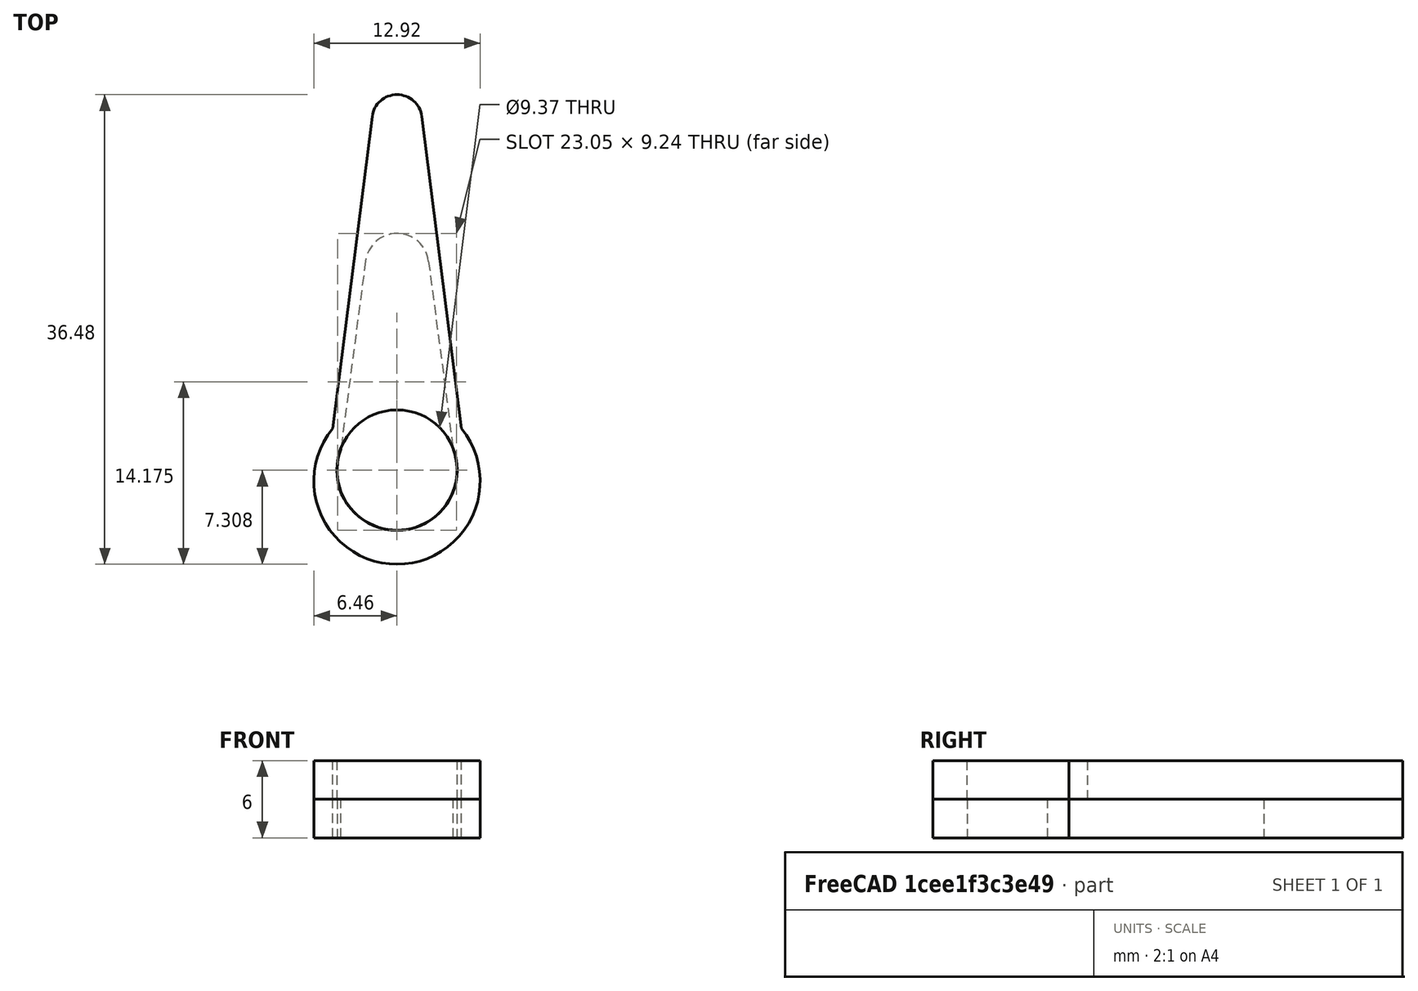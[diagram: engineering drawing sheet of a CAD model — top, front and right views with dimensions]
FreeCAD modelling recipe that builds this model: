
FCSTD DOCUMENT  (FreeCAD 0.18.4R)
Label: servo_pointer
License: All rights reserved
LicenseURL: http://en.wikipedia.org/wiki/All_rights_reserved
objects: Sketcher::SketchObject×2, PartDesign::Pad×2, PartDesign::Body×2, Mesh::Feature×1, Part::Compound×1, App::Part×1
note: 9 computed .brp shape members not serialized (recipe doc carries the construction recipe); baked Part::Feature solids carry a one-line shape summary decoded from their .brp

FEATURE [Mesh::Feature] ServoNeedle_Hole  label="ServoNeedle-Hole"
  Placement = pos=(0,0,2) rot=(0,0,1;0rad)
FEATURE [Sketcher::SketchObject] Sketch
  MapMode = 5
  Support = -> [XY_Plane001]
  sketch-geometry (8):
    g0: LineSegment StartX=-2.44767 StartY=16.3215 StartZ=0 EndX=-4.37 EndY=1.69 EndZ=0
    g1: LineSegment StartX=2.44767 StartY=16.3215 StartZ=0 EndX=4.37 EndY=1.69 EndZ=0
    g2: ArcOfCircle CenterX=2e-16 CenterY=0.0782726 CenterZ=0 NormalX=0 NormalY=0 NormalZ=1 AngleXU=0 Radius=4.65774 StartAngle=2.78825 EndAngle=6.63652
    g3: ArcOfCircle CenterX=1e-16 CenterY=15.9999 CenterZ=0 NormalX=0 NormalY=0 NormalZ=1 AngleXU=0 Radius=2.4687 StartAngle=0.130635 EndAngle=3.01096
    g4: ArcOfCircle CenterX=-3e-16 CenterY=-0.77104 CenterZ=0 NormalX=0 NormalY=0 NormalZ=1 AngleXU=0 Radius=6.46039 StartAngle=2.45585 EndAngle=6.96893
    g5: LineSegment StartX=-1.92828 StartY=27.554 StartZ=0 EndX=-5 EndY=3.32 EndZ=0
    g6: ArcOfCircle CenterX=-1e-16 CenterY=27.3096 CenterZ=0 NormalX=0 NormalY=0 NormalZ=1 AngleXU=0 Radius=1.94371 StartAngle=0.12608 EndAngle=3.01551
    g7: LineSegment StartX=1.92828 StartY=27.554 StartZ=0 EndX=5 EndY=3.32 EndZ=0
  constraints (16):
    c: Symmetric(g1,g0,g-2)
    c: Symmetric(g1,g0,g-2)
    c: Coincident(g2,g1)
    c: Coincident(g2,g0)
    c: Coincident(g3,g0)
    c: Tangent(g3,g1) = 1.5708
    c: Coincident(g4,g7)
    c: Coincident(g4,g5)
    c: Coincident(g6,g5)
    c: Tangent(g6,g7) = 1.5708
    c: Symmetric(g5,g6,g-2)
    c: Symmetric(g4,g4,g-2)
    c: DistanceX(g2,g4) = 5
    c: DistanceX(g2,g1) = 4.37
    c: DistanceY(g-1,g1) = 1.69
    c: DistanceY(g-1,g4) = 3.32
FEATURE [PartDesign::Pad] Pad
  Length = 3
  Length2 = 100
  Profile = -> Sketch
  Type = 0
FEATURE [PartDesign::Body] Body
  Group = -> [Sketch,Pad]
  Origin = -> Origin001
  Tip = -> Pad
FEATURE [Sketcher::SketchObject] Sketch001
  MapMode = 5
  Support = -> [XY_Plane001]
  sketch-geometry (5):
    g0: ArcOfCircle CenterX=-5e-16 CenterY=-0.77104 CenterZ=0 NormalX=0 NormalY=0 NormalZ=1 AngleXU=0 Radius=6.46039 StartAngle=2.45585 EndAngle=6.96893
    g1: LineSegment StartX=-1.92828 StartY=27.554 StartZ=0 EndX=-5 EndY=3.32 EndZ=0
    g2: ArcOfCircle CenterX=1e-16 CenterY=27.3096 CenterZ=0 NormalX=0 NormalY=0 NormalZ=1 AngleXU=0 Radius=1.94371 StartAngle=0.12608 EndAngle=3.01551
    g3: LineSegment StartX=1.92828 StartY=27.554 StartZ=0 EndX=5 EndY=3.32 EndZ=0
    g4: Circle CenterX=-2e-16 CenterY=0.0782726 CenterZ=0 NormalX=0 NormalY=0 NormalZ=1 AngleXU=0 Radius=4.68435
  constraints (7):
    c: Coincident(g0,g3)
    c: Coincident(g0,g1)
    c: Coincident(g2,g1)
    c: Tangent(g2,g3) = 1.5708
    c: Symmetric(g1,g2,g-2)
    c: Symmetric(g0,g0,g-2)
    c: DistanceY(g-1,g0) = 3.32
FEATURE [PartDesign::Pad] Pad001
  Length = 3
  Length2 = 100
  Profile = -> Sketch001
  Type = 0
FEATURE [PartDesign::Body] Body001
  Group = -> [Sketch001,Pad001]
  Origin = -> Origin002
  Placement = pos=(0,0,3) rot=(0,0,1;0rad)
  Tip = -> Pad001
FEATURE [Part::Compound] Compound
  Links = -> [Body001,Body]
FEATURE [App::Part] Part001  label="servo pointer top"
  Group = -> [Body001,Body,Compound]
  Origin = -> Origin003
  Placement = pos=(0,0,3) rot=(0,0,1;0rad)
